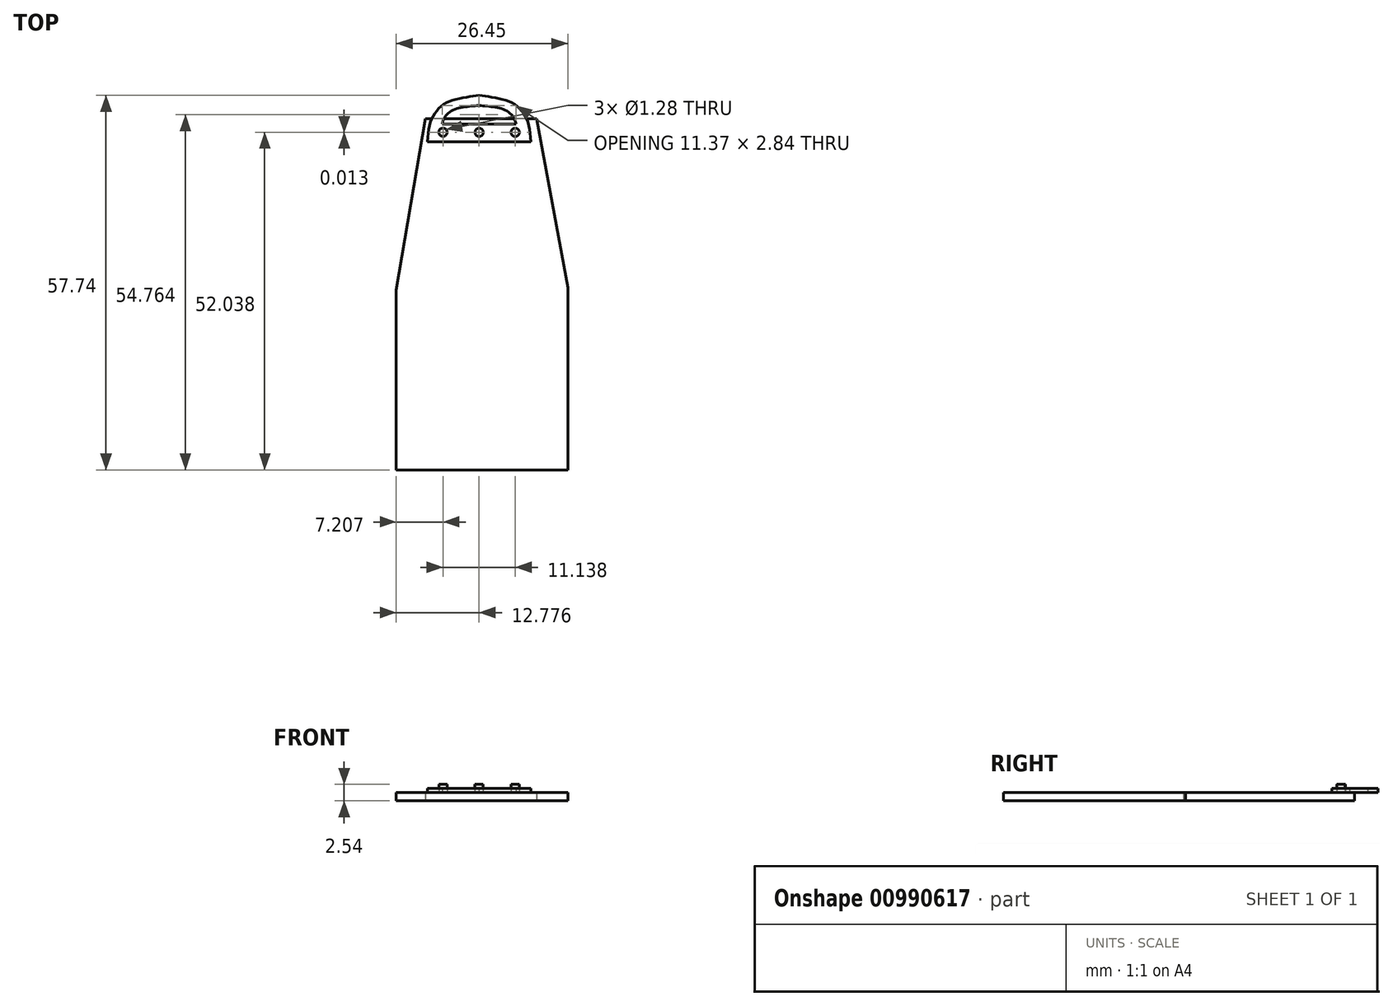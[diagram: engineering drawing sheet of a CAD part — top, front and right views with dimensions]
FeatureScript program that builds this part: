
annotation { "Feature Type Name" : "Feature", "Feature Type Description" : "" }
export const myFeature = defineFeature(function(context is Context, id is Id, definition is map)
    precondition{}
    {
        {
            var Q0;
            Q0=qCreatedBy(makeId("Top.planeOp"),FACE);
            var sketch = newSketch(context, id + "F0", { "sketchPlane" : qUnion([Q0])});
            skLineSegment(sketch, "E0", {"start": v(0, 27.75) * mm, "end": v(0, 0) * mm});
            skLineSegment(sketch, "E1", {"start": v(0, 0) * mm, "end": v(26.45, 0) * mm});
            skLineSegment(sketch, "E2", {"start": v(26.45, 0) * mm, "end": v(26.45, 28.11) * mm});
            skLineSegment(sketch, "E3", {"start": v(26.45, 28.11) * mm, "end": v(21.66, 54.1) * mm});
            skLineSegment(sketch, "E4", {"start": v(21.66, 54.1) * mm, "end": v(4.52, 54.1) * mm});
            skLineSegment(sketch, "E5", {"start": v(4.52, 54.1) * mm, "end": v(0, 27.75) * mm});
            skSolve(sketch);
        }
        {
            var Q0;
            Q0 = qSketchRegion(id + "F0", true);
            extrude(context, id + "F1", {"entities" : qUnion([Q0]), "depth" : 1.27 * mm, "offsetDistance" : 25.4 * mm});
        }
        {
            var Q0;
            Q0=makeQuery(id+"F1.opExtrude","CAP_FACE",FACE,{"disambiguationData":[OSD([sQuery(id+"F0.wireOp",EDGE,"E0"),sQuery(id+"F0.wireOp",EDGE,"E1"),sQuery(id+"F0.wireOp",EDGE,"E2"),sQuery(id+"F0.wireOp",EDGE,"E3"),sQuery(id+"F0.wireOp",EDGE,"E4"),sQuery(id+"F0.wireOp",EDGE,"E5")])],"isStart":false});
            var sketch = newSketch(context, id + "F2", { "sketchPlane" : qUnion([Q0])});
            skCircle(sketch, "E6", {"center": v(7.2, 52.05) * mm, "radius": 0.64 * mm});
            skCircle(sketch, "E7.1.0.0", {"center": v(12.78, 52.04) * mm, "radius": 0.64 * mm});
            skCircle(sketch, "E7.2.0.0", {"center": v(18.35, 52.04) * mm, "radius": 0.64 * mm});
            skLineSegment(sketch, "E7.direction1", {"start": v(7.2, 52.05) * mm, "end": v(12.78, 52.04) * mm, "construction": true});
            skSolve(sketch);
        }
        {
            var Q0;
            Q0=makeQuery(id+"F2.imprint","IMPRINT",FACE,{"disambiguationData":[TD([[makeQuery(id+"F2.imprint","IMPRINT",EDGE,{"derivedFrom":sQuery(id+"F2.wireOp",EDGE,"E6")}),1.0]])]});
            var Q1;
            Q1=makeQuery(id+"F2.imprint","IMPRINT",FACE,{"disambiguationData":[TD([[makeQuery(id+"F2.imprint","IMPRINT",EDGE,{"derivedFrom":sQuery(id+"F2.wireOp",EDGE,"E7.1.0.0")}),1.0]])]});
            var Q2;
            Q2=makeQuery(id+"F2.imprint","IMPRINT",FACE,{"disambiguationData":[TD([[makeQuery(id+"F2.imprint","IMPRINT",EDGE,{"derivedFrom":sQuery(id+"F2.wireOp",EDGE,"E7.2.0.0")}),1.0]])]});
            extrude(context, id + "F3", {"entities" : qUnion([Q0, Q1, Q2]), "operationType" : NewBodyOperationType.ADD, "depth" : 1.27 * mm, "offsetDistance" : 25.4 * mm});
        }
        {
            var Q0;
            Q0=makeQuery(id+"F1.opExtrude","CAP_FACE",FACE,{"disambiguationData":[OSD([sQuery(id+"F0.wireOp",EDGE,"E0"),sQuery(id+"F0.wireOp",EDGE,"E1"),sQuery(id+"F0.wireOp",EDGE,"E2"),sQuery(id+"F0.wireOp",EDGE,"E3"),sQuery(id+"F0.wireOp",EDGE,"E4"),sQuery(id+"F0.wireOp",EDGE,"E5")])],"isStart":false});
            var sketch = newSketch(context, id + "F4", { "sketchPlane" : qUnion([Q0])});
            skLineSegment(sketch, "E8", {"start": v(4.82, 50.6) * mm, "end": v(20.73, 50.6) * mm});
            skFitSpline(sketch, "E9", {"points": [v(20.73, 50.6) * mm, v(20.37, 53.33) * mm, v(19.54, 55.04) * mm, v(18.39, 56.28) * mm, v(16.62, 57.06) * mm, v(14.5, 57.51) * mm, v(12.78, 57.74) * mm], "startDerivative": vector(-1, 14.94) * mm, "endDerivative": vector(-10.37, 0.75) * mm});
            skLineSegment(sketch, "E10", {"start": v(12.78, 52.04) * mm, "end": v(12.78, 60.32) * mm, "construction": true});
            skFitSpline(sketch, "E11.MirrorCS", {"points": [v(4.82, 50.6) * mm, v(5.18, 53.33) * mm, v(6.01, 55.04) * mm, v(7.16, 56.28) * mm, v(8.94, 57.06) * mm, v(11.06, 57.51) * mm, v(12.78, 57.74) * mm], "startDerivative": vector(1, 14.94) * mm, "endDerivative": vector(10.37, 0.75) * mm});
            skLineSegment(sketch, "E12", {"start": v(7.1, 53.35) * mm, "end": v(12.78, 53.35) * mm});
            skFitSpline(sketch, "E13", {"points": [v(7.1, 53.35) * mm, v(7.65, 54.62) * mm, v(9.02, 55.58) * mm, v(10.85, 56) * mm, v(12.78, 56.18) * mm], "startDerivative": vector(1.76, 5.97) * mm, "endDerivative": vector(7.26, 0.53) * mm});
            skFitSpline(sketch, "E14.MirrorCS", {"points": [v(18.46, 53.35) * mm, v(17.9, 54.62) * mm, v(16.53, 55.58) * mm, v(14.7, 56) * mm, v(12.78, 56.18) * mm], "startDerivative": vector(-1.76, 5.97) * mm, "endDerivative": vector(-7.26, 0.53) * mm});
            skLineSegment(sketch, "E15.MirrorCS", {"start": v(18.46, 53.35) * mm, "end": v(12.78, 53.35) * mm});
            skSolve(sketch);
        }
        {
            var Q0;
            {var subQ7=sQuery(id+"F4.wireOp",EDGE,"E8");Q0=makeQuery(id+"F4.imprint","IMPRINT",FACE,{"disambiguationData":[TD([[makeQuery(id+"F4.imprint","IMPRINT",EDGE,{"derivedFrom":subQ7}),1.0]])]});}
            var Q1;
            {var subQ5=sQuery(id+"F4.wireOp",EDGE,"E11.MirrorCS");var subQ6=sQuery(id+"F4.wireOp",EDGE,"E9");var subQ7=makeQuery(id+"F4.imprint","INTERSECT",VERTEX,{"derivedFrom":[subQ6,subQ5]});Q1=makeQuery(id+"F4.imprint","IMPRINT",FACE,{"disambiguationData":[TD([[makeQuery(id+"F4.imprint","IMPRINT",EDGE,{"disambiguationData":[TD([[subQ7,1.0]])],"derivedFrom":subQ6}),1.0]])]});}
            extrude(context, id + "F5", {"entities" : qUnion([Q0, Q1]), "depth" : 0.64 * mm, "offsetDistance" : 25.4 * mm});
        }
    });
